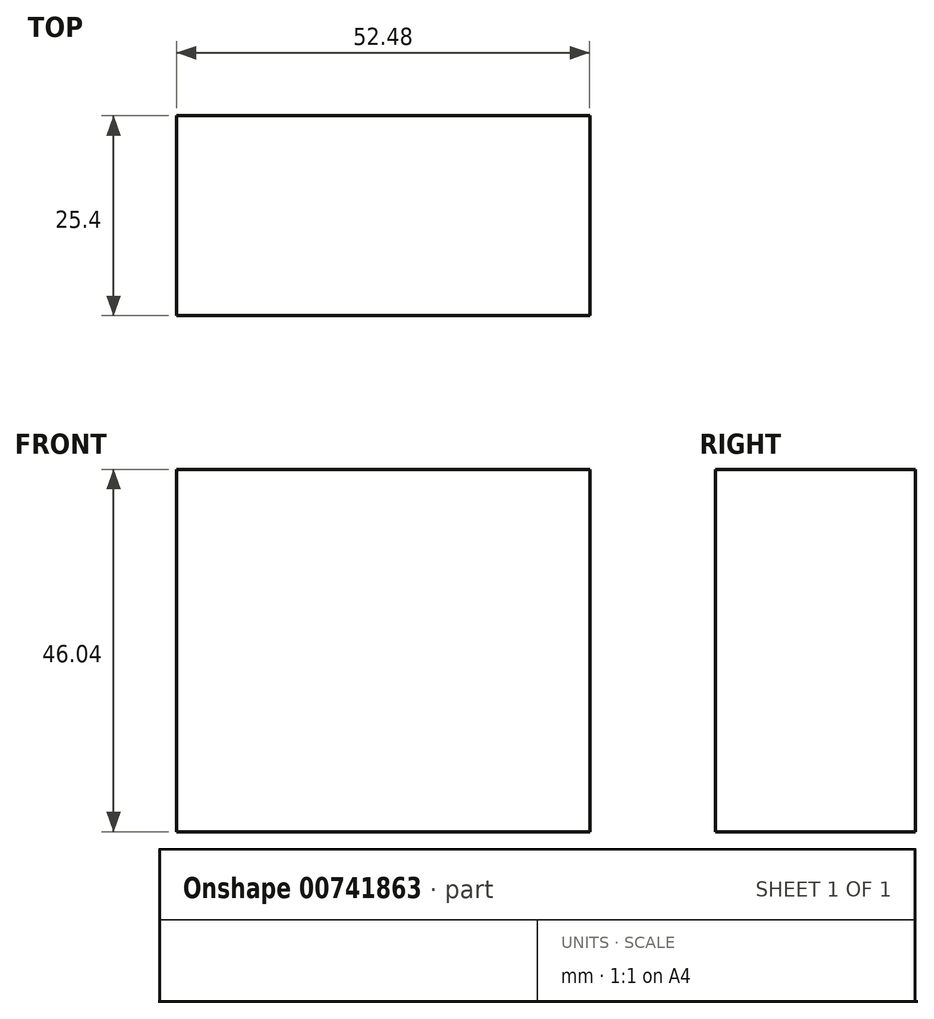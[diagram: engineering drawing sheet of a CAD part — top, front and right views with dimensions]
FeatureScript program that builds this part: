
annotation { "Feature Type Name" : "Feature", "Feature Type Description" : "" }
export const myFeature = defineFeature(function(context is Context, id is Id, definition is map)
    precondition{}
    {
        {
            var Q0;
            Q0=qCreatedBy(makeId("Front.planeOp"),FACE);
            var sketch = newSketch(context, id + "F0", { "sketchPlane" : qUnion([Q0])});
            skLineSegment(sketch, "E0.bottom", {"start": v(0, -6.59) * mm, "end": v(52.48, -6.59) * mm});
            skLineSegment(sketch, "E0.top", {"start": v(0, -52.63) * mm, "end": v(52.48, -52.63) * mm});
            skLineSegment(sketch, "E0.left", {"start": v(0, -6.59) * mm, "end": v(0, -52.63) * mm});
            skLineSegment(sketch, "E0.right", {"start": v(52.48, -6.59) * mm, "end": v(52.48, -52.63) * mm});
            skSolve(sketch);
        }
        {
            var Q0;
            Q0=makeQuery(id+"F0.imprint","IMPRINT",FACE,{"disambiguationData":[TD([[makeQuery(id+"F0.imprint","IMPRINT",EDGE,{"derivedFrom":sQuery(id+"F0.wireOp",EDGE,"E0.bottom")}),-1.0]])]});
            extrude(context, id + "F1", {"entities" : qUnion([Q0]), "depth" : 25.4 * mm, "offsetDistance" : 25.4 * mm});
        }
    });
